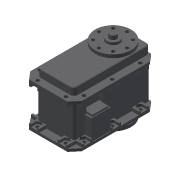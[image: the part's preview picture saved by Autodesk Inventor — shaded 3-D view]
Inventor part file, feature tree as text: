
AUTODESK INVENTOR PART (.ipt)
format: ipt  version: 2020 (Build 240168000, 168)  size: 723,456 bytes
history: native  units: mm (DEFAULTED — no unit token found)
features: other x6, sketch x3, extrude x2
ambient origin geometry x8: Origin, YZ Plane, XZ Plane, XY Plane, X Axis, Y Axis, Z Axis, Center Point
bodies: Body1 (feature_tree)
feature tree (11):
  other  "솔리드1"
  other  "기준1"
  sketch  "스케치1"
  other  "작업 평면1"
  other  "작업 평면2"
  other  "작업 평면3"
  extrude  "돌출1"  [1 undecoded]
  extrude  "돌출2"  [1 undecoded]
  other  "작업 평면4"
  sketch  "스케치2"
  sketch  "스케치3"
note: 2 required parameter values undecoded (feature->parameter linkage not recoverable at this tier; creation-order binding heuristic only, values carry confidence <= 0.55)
